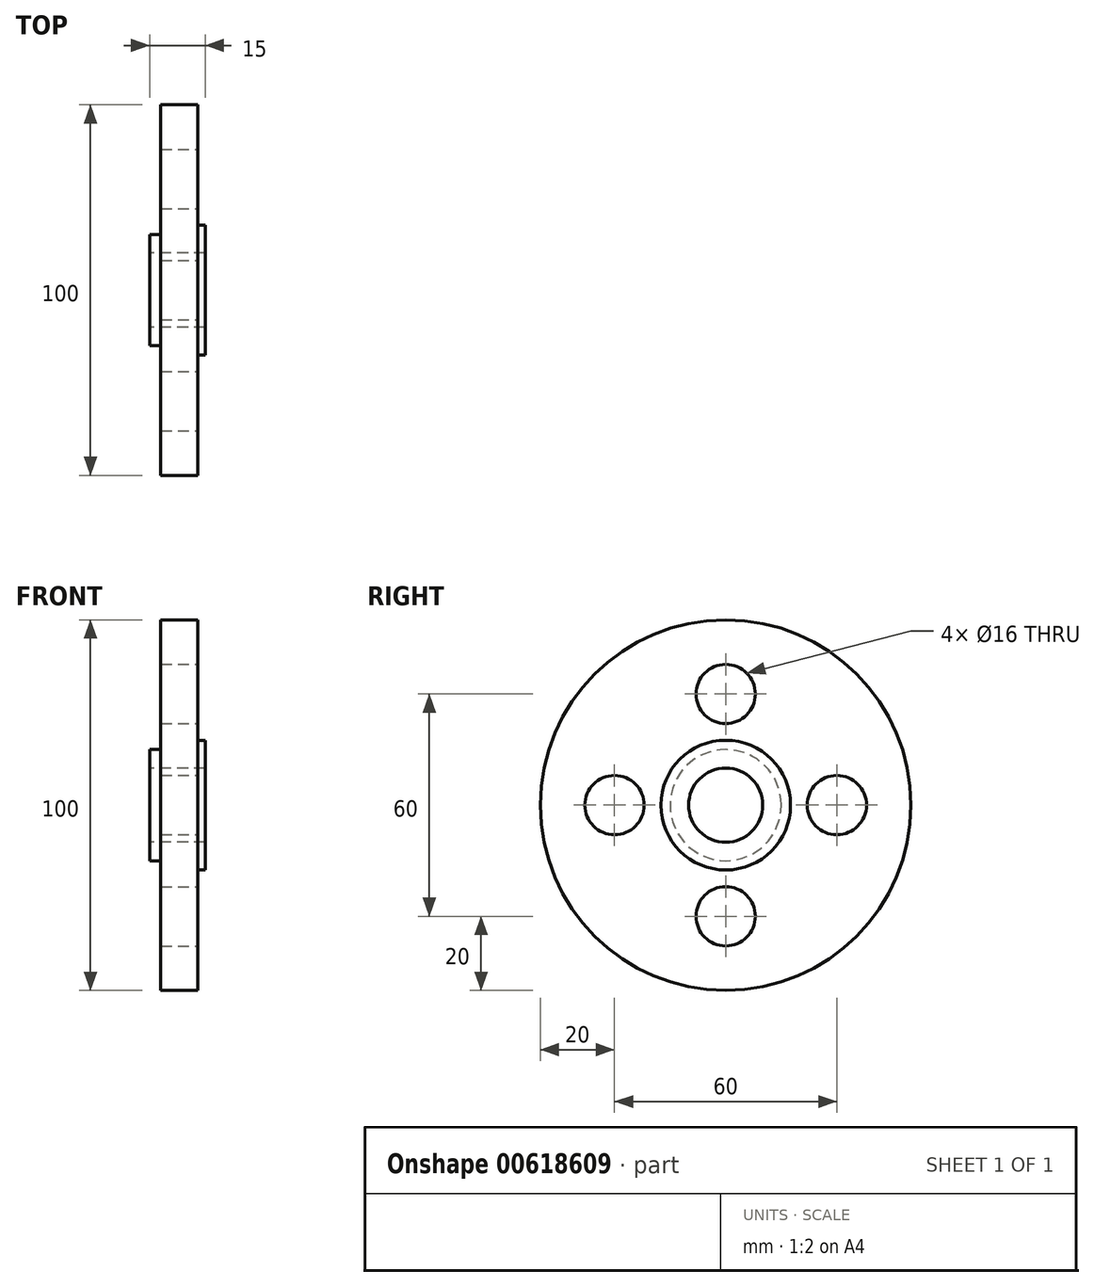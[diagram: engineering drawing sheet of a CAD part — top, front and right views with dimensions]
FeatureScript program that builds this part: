
annotation { "Feature Type Name" : "Feature", "Feature Type Description" : "" }
export const myFeature = defineFeature(function(context is Context, id is Id, definition is map)
    precondition{}
    {
        {
            var Q0;
            Q0=qCreatedBy(makeId("Front.planeOp"),FACE);
            var sketch = newSketch(context, id + "F0", { "sketchPlane" : qUnion([Q0])});
            skLineSegment(sketch, "E0", {"start": v(-7.8, 0) * mm, "end": v(23.92, 0) * mm, "construction": true});
            skLineSegment(sketch, "E1", {"start": v(0, 10) * mm, "end": v(0, 15) * mm});
            skLineSegment(sketch, "E2", {"start": v(0, 15) * mm, "end": v(3, 15) * mm});
            skLineSegment(sketch, "E3", {"start": v(3, 15) * mm, "end": v(3, 50) * mm});
            skLineSegment(sketch, "E4", {"start": v(3, 50) * mm, "end": v(13, 50) * mm});
            skLineSegment(sketch, "E5", {"start": v(13, 50) * mm, "end": v(13, 17.5) * mm});
            skLineSegment(sketch, "E6", {"start": v(13, 17.5) * mm, "end": v(15, 17.5) * mm});
            skLineSegment(sketch, "E7", {"start": v(15, 17.5) * mm, "end": v(15, 10) * mm});
            skLineSegment(sketch, "E8", {"start": v(15, 10) * mm, "end": v(0, 10) * mm});
            skSolve(sketch);
        }
        {
            var Q0;
            Q0 = qSketchRegion(id + "F0", true);
            var Q1;
            Q1=sQuery(id+"F0.wireOp",EDGE,"E0");
            revolve(context, id + "F1", {"entities" : qUnion([Q0]), "axis" : qUnion([Q1]), "revolveType" : RevolveType.FULL});
        }
        {
            var Q0;
            Q0=makeQuery(id+"F1.opRevolve","SWEPT_FACE",FACE,{"disambiguationData":[OSD([sQuery(id+"F0.wireOp",EDGE,"E5")])]});
            var sketch = newSketch(context, id + "F2", { "sketchPlane" : qUnion([Q0])});
            skCircle(sketch, "E9", {"center": v(0, 0) * mm, "radius": 30 * mm, "construction": true});
            skCircle(sketch, "E10", {"center": v(0, 30) * mm, "radius": 8 * mm});
            skCircle(sketch, "E11.1.0", {"center": v(-30, 0) * mm, "radius": 8 * mm});
            skCircle(sketch, "E11.2.0", {"center": v(0, -30) * mm, "radius": 8 * mm});
            skCircle(sketch, "E11.3.0", {"center": v(30, 0) * mm, "radius": 8 * mm});
            skSolve(sketch);
        }
        {
            var Q0;
            Q0 = qSketchRegion(id + "F2", true);
            extrude(context, id + "F3", {"entities" : qUnion([Q0]), "operationType" : NewBodyOperationType.REMOVE, "endBound" : BoundingType.THROUGH_ALL, "oppositeDirection" : true, "depth" : 25 * mm, "offsetDistance" : 25 * mm});
        }
    });
